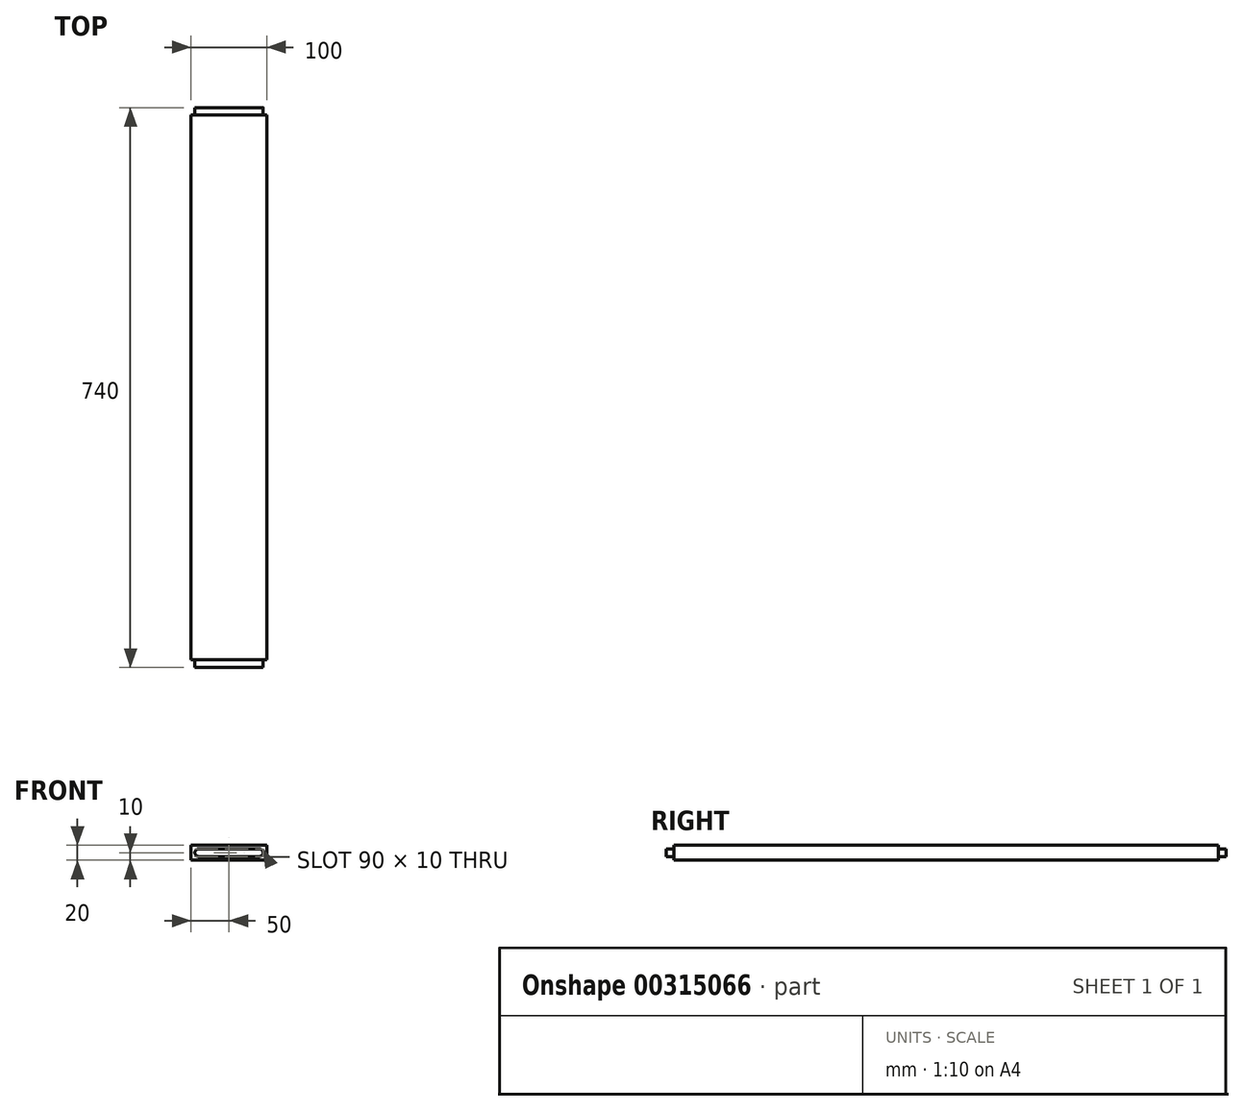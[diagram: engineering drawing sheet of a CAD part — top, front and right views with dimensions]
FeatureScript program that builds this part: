
annotation { "Feature Type Name" : "Feature", "Feature Type Description" : "" }
export const myFeature = defineFeature(function(context is Context, id is Id, definition is map)
    precondition{}
    {
        {
            var Q0;
            Q0=qCreatedBy(makeId("Front.planeOp"),FACE);
            var sketch = newSketch(context, id + "F0", { "sketchPlane" : qUnion([Q0])});
            skLineSegment(sketch, "E0.bottom", {"start": v(50, 10) * mm, "end": v(-50, 10) * mm});
            skLineSegment(sketch, "E0.top", {"start": v(50, -10) * mm, "end": v(-50, -10) * mm});
            skLineSegment(sketch, "E0.left", {"start": v(50, 10) * mm, "end": v(50, -10) * mm});
            skLineSegment(sketch, "E0.right", {"start": v(-50, 10) * mm, "end": v(-50, -10) * mm});
            skPoint(sketch, "E0.middle", {"position": v(0, 0) * mm});
            skLineSegment(sketch, "E1.0", {"start": v(40, 5) * mm, "end": v(-40, 5) * mm});
            skLineSegment(sketch, "E1.1", {"start": v(45, 0) * mm, "end": v(45, 0) * mm});
            skLineSegment(sketch, "E1.2", {"start": v(40, -5) * mm, "end": v(-40, -5) * mm});
            skLineSegment(sketch, "E1.3", {"start": v(-45, 0) * mm, "end": v(-45, 0) * mm});
            skPoint(sketch, "E2.visualSharp", {"position": v(45, 5) * mm});
            skArc(sketch, "E2.filletArc", {"start": v(45, 0) * mm, "mid": v(43.54, 3.54) * mm, "end": v(40, 5) * mm});
            skPoint(sketch, "E3.visualSharp", {"position": v(45, -5) * mm});
            skArc(sketch, "E3.filletArc", {"start": v(40, -5) * mm, "mid": v(43.54, -3.54) * mm, "end": v(45, 0) * mm});
            skPoint(sketch, "E4.visualSharp", {"position": v(-45, 5) * mm});
            skArc(sketch, "E4.filletArc", {"start": v(-40, 5) * mm, "mid": v(-43.54, 3.54) * mm, "end": v(-45, 0) * mm});
            skPoint(sketch, "E5.visualSharp", {"position": v(-45, -5) * mm});
            skArc(sketch, "E5.filletArc", {"start": v(-45, 0) * mm, "mid": v(-43.54, -3.54) * mm, "end": v(-40, -5) * mm});
            skSolve(sketch);
        }
        {
            var Q0;
            Q0=makeQuery(id+"F0.imprint","IMPRINT",FACE,{"disambiguationData":[TD([[makeQuery(id+"F0.imprint","IMPRINT",EDGE,{"derivedFrom":sQuery(id+"F0.wireOp",EDGE,"E0.bottom")}),1.0]])]});
            var Q1;
            Q1=makeQuery(id+"F0.imprint","IMPRINT",FACE,{"disambiguationData":[TD([[makeQuery(id+"F0.imprint","IMPRINT",EDGE,{"derivedFrom":sQuery(id+"F0.wireOp",EDGE,"E1.0")}),1.0]])]});
            var Q2;
            Q2=sQuery(id+"F0.wireOp",EDGE,"E0.left");
            var Q3;
            Q3=sQuery(id+"F0.wireOp",EDGE,"E0.bottom");
            var Q4;
            Q4=sQuery(id+"F0.wireOp",EDGE,"E0.top");
            var Q5;
            Q5=sQuery(id+"F0.wireOp",EDGE,"E0.right");
            extrude(context, id + "F1", {"entities" : qUnion([Q0, Q1]), "surfaceEntities" : qUnion([Q2, Q3, Q4, Q5]), "depth" : 720 * mm});
        }
        {
            var Q0;
            Q0=makeQuery(id+"F0.imprint","IMPRINT",FACE,{"disambiguationData":[TD([[makeQuery(id+"F0.imprint","IMPRINT",EDGE,{"derivedFrom":sQuery(id+"F0.wireOp",EDGE,"E1.0")}),1.0]])]});
            extrude(context, id + "F2", {"entities" : qUnion([Q0]), "operationType" : NewBodyOperationType.ADD, "oppositeDirection" : true, "depth" : 10 * mm});
        }
        {
            var Q0;
            Q0=makeQuery(id+"F0.imprint","IMPRINT",FACE,{"disambiguationData":[TD([[makeQuery(id+"F0.imprint","IMPRINT",EDGE,{"derivedFrom":sQuery(id+"F0.wireOp",EDGE,"E1.0")}),1.0]])]});
            extrude(context, id + "F3", {"entities" : qUnion([Q0]), "operationType" : NewBodyOperationType.ADD, "depth" : 730 * mm});
        }
    });
